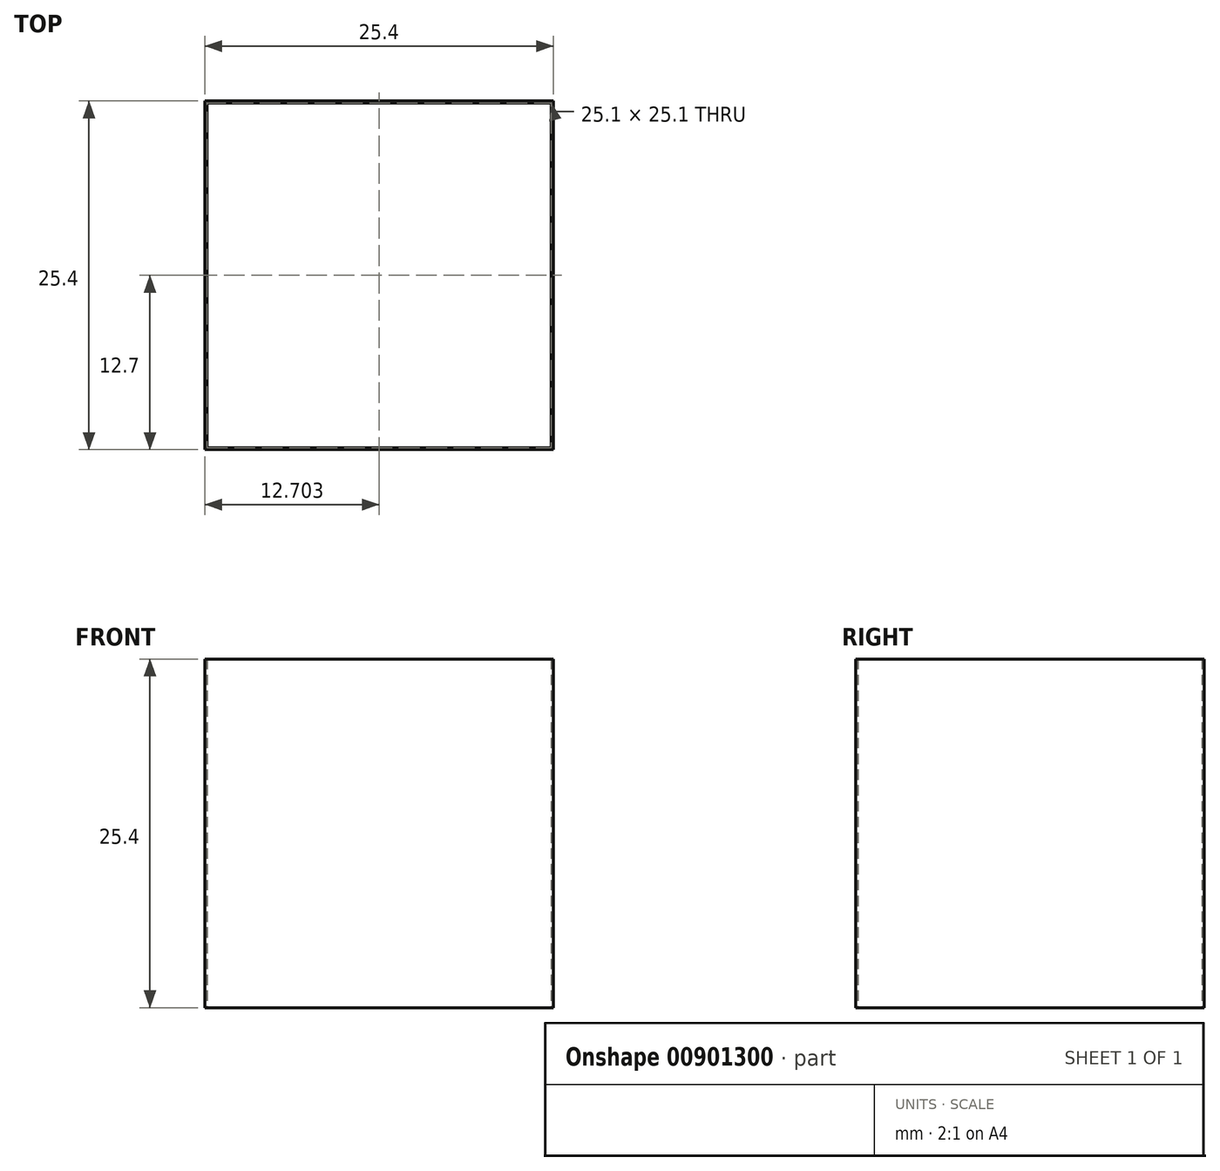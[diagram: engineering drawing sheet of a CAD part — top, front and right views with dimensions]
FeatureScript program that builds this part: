
annotation { "Feature Type Name" : "Feature", "Feature Type Description" : "" }
export const myFeature = defineFeature(function(context is Context, id is Id, definition is map)
    precondition{}
    {
        {
            var Q0;
            Q0=qCreatedBy(makeId("Top.planeOp"),FACE);
            var sketch = newSketch(context, id + "F0", { "sketchPlane" : qUnion([Q0])});
            skLineSegment(sketch, "E0.bottom", {"start": v(-34.47, 33.42) * mm, "end": v(-9.07, 33.42) * mm});
            skLineSegment(sketch, "E0.top", {"start": v(-34.47, 8.02) * mm, "end": v(-9.07, 8.02) * mm});
            skLineSegment(sketch, "E0.left", {"start": v(-34.47, 33.42) * mm, "end": v(-34.47, 8.02) * mm});
            skLineSegment(sketch, "E0.right", {"start": v(-9.07, 33.42) * mm, "end": v(-9.07, 8.02) * mm});
            skLineSegment(sketch, "E1.0", {"start": v(-34.32, 33.27) * mm, "end": v(-9.22, 33.27) * mm});
            skLineSegment(sketch, "E1.1", {"start": v(-34.32, 33.27) * mm, "end": v(-34.32, 8.17) * mm});
            skLineSegment(sketch, "E1.2", {"start": v(-34.32, 8.17) * mm, "end": v(-9.22, 8.17) * mm});
            skLineSegment(sketch, "E1.3", {"start": v(-9.22, 33.27) * mm, "end": v(-9.22, 8.17) * mm});
            skSolve(sketch);
        }
        {
            var Q0;
            Q0 = qSketchRegion(id + "F0", true);
            extrude(context, id + "F1", {"entities" : qUnion([Q0]), "depth" : 25.4 * mm, "offsetDistance" : 25.4 * mm});
        }
    });
